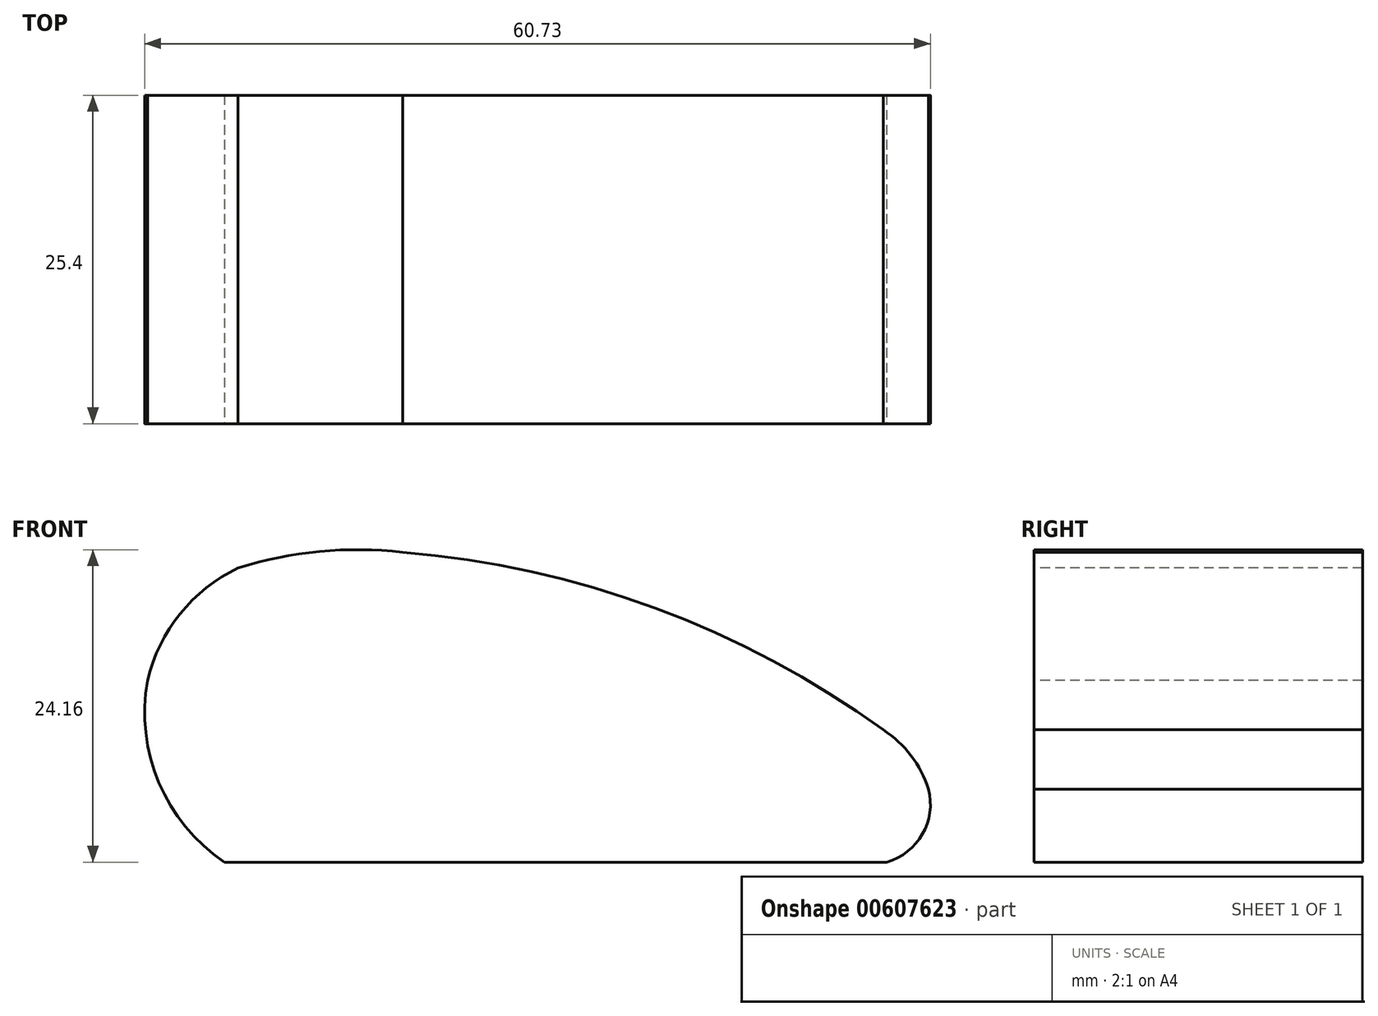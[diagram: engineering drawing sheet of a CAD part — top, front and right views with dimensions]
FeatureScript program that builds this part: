
annotation { "Feature Type Name" : "Feature", "Feature Type Description" : "" }
export const myFeature = defineFeature(function(context is Context, id is Id, definition is map)
    precondition{}
    {
        {
            var Q0;
            Q0=qCreatedBy(makeId("Front.planeOp"),FACE);
            var sketch = newSketch(context, id + "F0", { "sketchPlane" : qUnion([Q0])});
            skLineSegment(sketch, "E0", {"start": v(13.7, -62.77) * mm, "end": v(-37.51, -62.77) * mm});
            skArc(sketch, "E1", {"start": v(-43.43, -48.7) * mm, "mid": v(-42.56, -56.62) * mm, "end": v(-37.51, -62.77) * mm});
            skArc(sketch, "E2", {"start": v(-36.44, -40.03) * mm, "mid": v(-40.92, -43.57) * mm, "end": v(-43.43, -48.7) * mm});
            skArc(sketch, "E3", {"start": v(-23.72, -38.81) * mm, "mid": v(-30.14, -38.74) * mm, "end": v(-36.44, -40.03) * mm});
            skArc(sketch, "E4", {"start": v(13.42, -52.54) * mm, "mid": v(-4.2, -43.12) * mm, "end": v(-23.72, -38.81) * mm});
            skArc(sketch, "E5", {"start": v(16.92, -57.12) * mm, "mid": v(15.57, -54.52) * mm, "end": v(13.42, -52.54) * mm});
            skArc(sketch, "E6", {"start": v(13.7, -62.77) * mm, "mid": v(16.46, -60.6) * mm, "end": v(16.92, -57.12) * mm});
            skSolve(sketch);
        }
        {
            var Q0;
            Q0=makeQuery(id+"F0.imprint","IMPRINT",FACE,{"disambiguationData":[TD([[makeQuery(id+"F0.imprint","IMPRINT",EDGE,{"derivedFrom":sQuery(id+"F0.wireOp",EDGE,"E0")}),-1.0]])]});
            var Q1;
            Q1=sQuery(id+"F0.wireOp",EDGE,"E4");
            var Q2;
            Q2=sQuery(id+"F0.wireOp",EDGE,"E6");
            var Q3;
            Q3=sQuery(id+"F0.wireOp",EDGE,"E5");
            var Q4;
            Q4=sQuery(id+"F0.wireOp",EDGE,"E0");
            var Q5;
            Q5=sQuery(id+"F0.wireOp",EDGE,"E1");
            var Q6;
            Q6=sQuery(id+"F0.wireOp",EDGE,"E2");
            var Q7;
            Q7=sQuery(id+"F0.wireOp",EDGE,"E3");
            extrude(context, id + "F1", {"entities" : qUnion([Q0]), "bodyType" : ToolBodyType.SURFACE, "surfaceEntities" : qUnion([Q1, Q2, Q3, Q4, Q5, Q6, Q7]), "depth" : 25.4 * mm, "offsetDistance" : 25.4 * mm});
        }
    });
